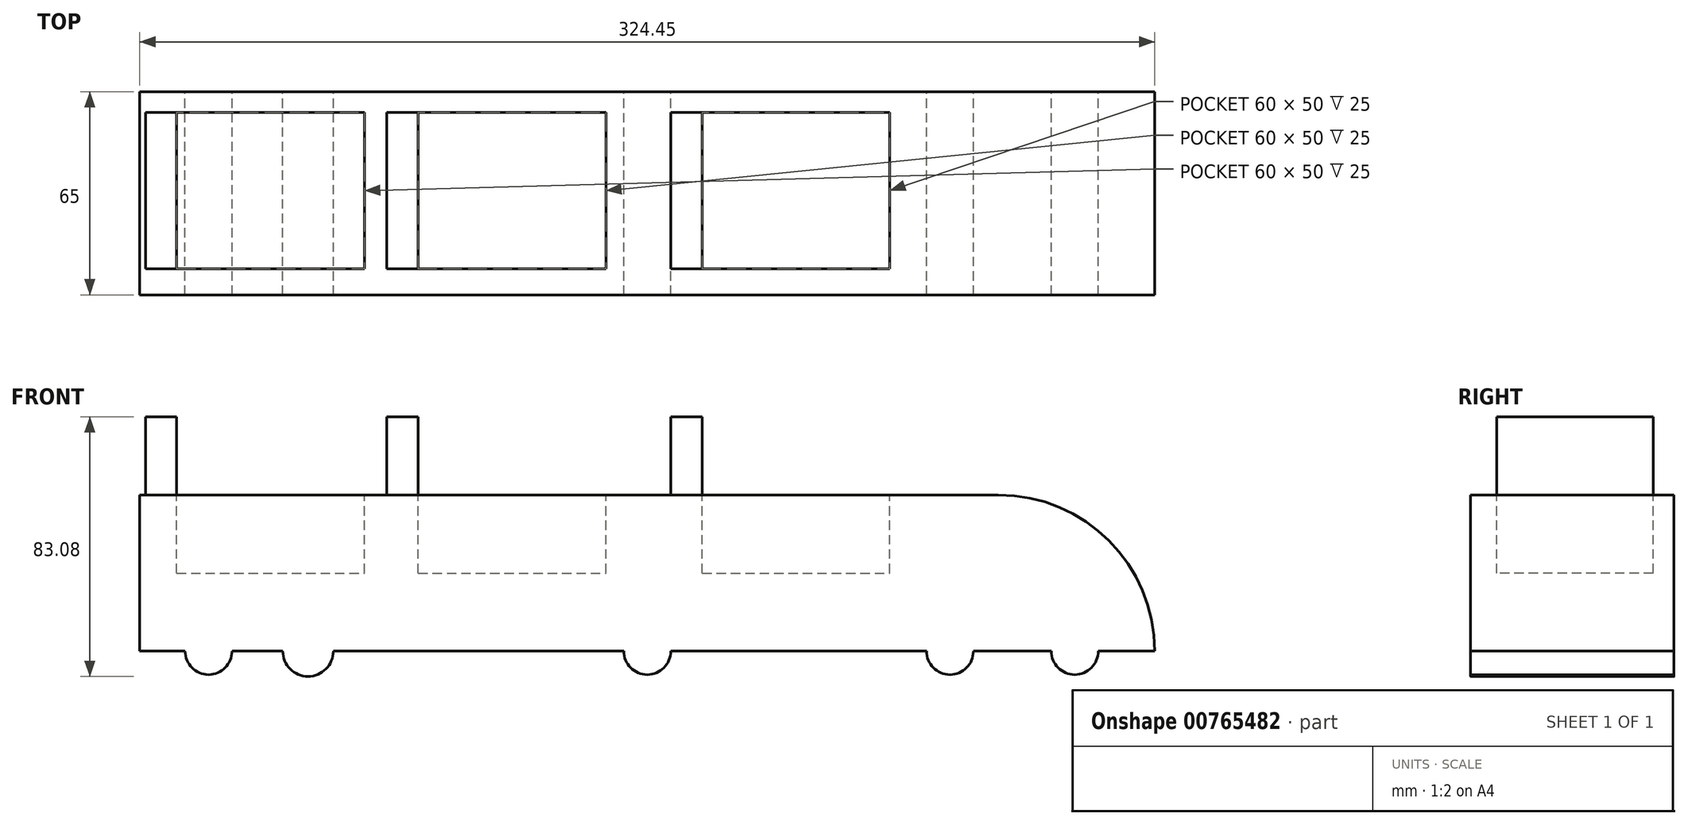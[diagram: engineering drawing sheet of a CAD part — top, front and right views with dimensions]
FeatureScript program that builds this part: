
annotation { "Feature Type Name" : "Feature", "Feature Type Description" : "" }
export const myFeature = defineFeature(function(context is Context, id is Id, definition is map)
    precondition{}
    {
        {
            var Q0;
            Q0=qCreatedBy(makeId("Top.planeOp"),FACE);
            var sketch = newSketch(context, id + "F0", { "sketchPlane" : qUnion([Q0])});
            skLineSegment(sketch, "E0.bottom", {"start": v(-92.43, -16.82) * mm, "end": v(232.02, -16.82) * mm});
            skLineSegment(sketch, "E0.top", {"start": v(-92.43, -81.82) * mm, "end": v(232.02, -81.82) * mm});
            skLineSegment(sketch, "E0.left", {"start": v(-92.43, -16.82) * mm, "end": v(-92.43, -81.82) * mm});
            skLineSegment(sketch, "E0.right", {"start": v(232.02, -16.82) * mm, "end": v(232.02, -81.82) * mm});
            skSolve(sketch);
        }
        {
            var Q0;
            Q0 = qSketchRegion(id + "F0", true);
            extrude(context, id + "F1", {"entities" : qUnion([Q0]), "depth" : 50 * mm, "offsetDistance" : 25 * mm});
        }
        {
            var Q0;
            Q0=makeQuery(id+"F1.opExtrude","CAP_EDGE",EDGE,{"disambiguationData":[OSD([sQuery(id+"F0.wireOp",EDGE,"E0.right")])],"isStart":false});
            fillet(context, id + "F2", {"entities" : qUnion([Q0]), "radius" : 50 * mm, "tangentPropagation" : true, "allowEdgeOverflow" : false});
        }
        {
            var Q0;
            Q0=makeQuery(id+"F1.opExtrude","CAP_FACE",FACE,{"disambiguationData":[OSD([sQuery(id+"F0.wireOp",EDGE,"E0.bottom"),sQuery(id+"F0.wireOp",EDGE,"E0.top"),sQuery(id+"F0.wireOp",EDGE,"E0.left"),sQuery(id+"F0.wireOp",EDGE,"E0.right")])],"isStart":false});
            var sketch = newSketch(context, id + "F3", { "sketchPlane" : qUnion([Q0])});
            skLineSegment(sketch, "E1.bottom", {"start": v(-80.63, -23.44) * mm, "end": v(-20.63, -23.44) * mm});
            skLineSegment(sketch, "E1.top", {"start": v(-80.63, -73.44) * mm, "end": v(-20.63, -73.44) * mm});
            skLineSegment(sketch, "E1.left", {"start": v(-80.63, -23.44) * mm, "end": v(-80.63, -73.44) * mm});
            skLineSegment(sketch, "E1.right", {"start": v(-20.63, -23.44) * mm, "end": v(-20.63, -73.44) * mm});
            skLineSegment(sketch, "E2.bottom", {"start": v(-3.45, -23.44) * mm, "end": v(56.55, -23.44) * mm});
            skLineSegment(sketch, "E2.top", {"start": v(-3.45, -73.44) * mm, "end": v(56.55, -73.44) * mm});
            skLineSegment(sketch, "E2.left", {"start": v(-3.45, -23.44) * mm, "end": v(-3.45, -73.44) * mm});
            skLineSegment(sketch, "E2.right", {"start": v(56.55, -23.44) * mm, "end": v(56.55, -73.44) * mm});
            skLineSegment(sketch, "E3.bottom", {"start": v(87.33, -23.44) * mm, "end": v(147.33, -23.44) * mm});
            skLineSegment(sketch, "E3.top", {"start": v(87.33, -73.44) * mm, "end": v(147.33, -73.44) * mm});
            skLineSegment(sketch, "E3.left", {"start": v(87.33, -23.44) * mm, "end": v(87.33, -73.44) * mm});
            skLineSegment(sketch, "E3.right", {"start": v(147.33, -23.44) * mm, "end": v(147.33, -73.44) * mm});
            skSolve(sketch);
        }
        {
            var Q0;
            Q0=makeQuery(id+"F3.imprint","IMPRINT",FACE,{"disambiguationData":[TD([[makeQuery(id+"F3.imprint","IMPRINT",EDGE,{"derivedFrom":sQuery(id+"F3.wireOp",EDGE,"E1.bottom")}),-1.0]])]});
            var Q1;
            Q1=makeQuery(id+"F3.imprint","IMPRINT",FACE,{"disambiguationData":[TD([[makeQuery(id+"F3.imprint","IMPRINT",EDGE,{"derivedFrom":sQuery(id+"F3.wireOp",EDGE,"E2.bottom")}),-1.0]])]});
            var Q2;
            Q2=makeQuery(id+"F3.imprint","IMPRINT",FACE,{"disambiguationData":[TD([[makeQuery(id+"F3.imprint","IMPRINT",EDGE,{"derivedFrom":sQuery(id+"F3.wireOp",EDGE,"E3.bottom")}),-1.0]])]});
            extrude(context, id + "F4", {"entities" : qUnion([Q0, Q1, Q2]), "operationType" : NewBodyOperationType.REMOVE, "oppositeDirection" : true, "depth" : 25 * mm, "offsetDistance" : 25 * mm});
        }
        {
            var Q0;
            Q0=makeQuery(id+"F1.opExtrude","SWEPT_FACE",FACE,{"disambiguationData":[OSD([sQuery(id+"F0.wireOp",EDGE,"E0.top")])]});
            var sketch = newSketch(context, id + "F5", { "sketchPlane" : qUnion([Q0])});
            skCircle(sketch, "E4", {"center": v(-77.66, 0) * mm, "radius": 7.5 * mm});
            skCircle(sketch, "E5", {"center": v(-29.66, 0) * mm, "radius": 7.5 * mm});
            skCircle(sketch, "E6", {"center": v(204.34, 0) * mm, "radius": 7.5 * mm});
            skCircle(sketch, "E7", {"center": v(157.84, 0) * mm, "radius": 7.5 * mm});
            skSolve(sketch);
        }
        {
            var Q0;
            {var subQ0=sQuery(id+"F5.wireOp",EDGE,"E6");var subQ1=makeQuery(id+"F1.opExtrude","CAP_EDGE",EDGE,{"disambiguationData":[OSD([sQuery(id+"F0.wireOp",EDGE,"E0.top")])],"isStart":true});var subQ2=makeQuery(id+"F5.imprint","INTERSECT",VERTEX,{"disambiguationData":[OD(0.0)],"derivedFrom":[subQ1,subQ0]});Q0=makeQuery(id+"F5.imprint","IMPRINT",FACE,{"disambiguationData":[TD([[makeQuery(id+"F5.imprint","IMPRINT",EDGE,{"disambiguationData":[TD([[subQ2,1.0]])],"derivedFrom":subQ0}),1.0]])]});}
            var Q1;
            {var subQ0=sQuery(id+"F5.wireOp",EDGE,"E7");var subQ1=makeQuery(id+"F1.opExtrude","CAP_EDGE",EDGE,{"disambiguationData":[OSD([sQuery(id+"F0.wireOp",EDGE,"E0.top")])],"isStart":true});var subQ2=makeQuery(id+"F5.imprint","INTERSECT",VERTEX,{"disambiguationData":[OD(0.0)],"derivedFrom":[subQ1,subQ0]});Q1=makeQuery(id+"F5.imprint","IMPRINT",FACE,{"disambiguationData":[TD([[makeQuery(id+"F5.imprint","IMPRINT",EDGE,{"disambiguationData":[TD([[subQ2,1.0]])],"derivedFrom":subQ0}),1.0]])]});}
            var Q2;
            {var subQ0=sQuery(id+"F5.wireOp",EDGE,"E5");var subQ1=makeQuery(id+"F1.opExtrude","CAP_EDGE",EDGE,{"disambiguationData":[OSD([sQuery(id+"F0.wireOp",EDGE,"E0.top")])],"isStart":true});var subQ2=makeQuery(id+"F5.imprint","INTERSECT",VERTEX,{"disambiguationData":[OD(0.0)],"derivedFrom":[subQ1,subQ0]});Q2=makeQuery(id+"F5.imprint","IMPRINT",FACE,{"disambiguationData":[TD([[makeQuery(id+"F5.imprint","IMPRINT",EDGE,{"disambiguationData":[TD([[subQ2,-1.0]])],"derivedFrom":subQ0}),1.0]])]});}
            var Q3;
            {var subQ0=sQuery(id+"F5.wireOp",EDGE,"E4");var subQ1=makeQuery(id+"F1.opExtrude","CAP_EDGE",EDGE,{"disambiguationData":[OSD([sQuery(id+"F0.wireOp",EDGE,"E0.top")])],"isStart":true});var subQ2=makeQuery(id+"F5.imprint","INTERSECT",VERTEX,{"disambiguationData":[OD(0.0)],"derivedFrom":[subQ1,subQ0]});Q3=makeQuery(id+"F5.imprint","IMPRINT",FACE,{"disambiguationData":[TD([[makeQuery(id+"F5.imprint","IMPRINT",EDGE,{"disambiguationData":[TD([[subQ2,-1.0]])],"derivedFrom":subQ0}),1.0]])]});}
            extrude(context, id + "F6", {"entities" : qUnion([Q0, Q1, Q2, Q3]), "operationType" : NewBodyOperationType.REMOVE, "depth" : 65 * mm, "offsetDistance" : 25 * mm});
        }
        {
            var Q0;
            Q0=makeQuery(id+"F1.opExtrude","SWEPT_FACE",FACE,{"disambiguationData":[OSD([sQuery(id+"F0.wireOp",EDGE,"E0.bottom")])]});
            var sketch = newSketch(context, id + "F7", { "sketchPlane" : qUnion([Q0])});
            skCircle(sketch, "E8", {"center": v(-206.44, 0) * mm, "radius": 7.5 * mm});
            skCircle(sketch, "E9", {"center": v(-166.54, 0) * mm, "radius": 7.5 * mm});
            skCircle(sketch, "E10", {"center": v(70.46, 0) * mm, "radius": 7.5 * mm});
            skCircle(sketch, "E11", {"center": v(38.66, 0) * mm, "radius": 8.08 * mm});
            skCircle(sketch, "E12", {"center": v(-69.8, 0) * mm, "radius": 7.5 * mm});
            skSolve(sketch);
        }
        {
            var Q0;
            {var subQ0=sQuery(id+"F7.wireOp",EDGE,"E8");var subQ1=makeQuery(id+"F1.opExtrude","CAP_EDGE",EDGE,{"disambiguationData":[OSD([sQuery(id+"F0.wireOp",EDGE,"E0.bottom")])],"isStart":true});var subQ2=makeQuery(id+"F7.imprint","INTERSECT",VERTEX,{"disambiguationData":[OD(0.0)],"derivedFrom":[subQ1,subQ0]});Q0=makeQuery(id+"F7.imprint","IMPRINT",FACE,{"disambiguationData":[TD([[makeQuery(id+"F7.imprint","IMPRINT",EDGE,{"disambiguationData":[TD([[subQ2,-1.0]])],"derivedFrom":subQ0}),1.0]])]});}
            var Q1;
            {var subQ0=sQuery(id+"F7.wireOp",EDGE,"E9");var subQ1=makeQuery(id+"F1.opExtrude","CAP_EDGE",EDGE,{"disambiguationData":[OSD([sQuery(id+"F0.wireOp",EDGE,"E0.bottom")])],"isStart":true});var subQ2=makeQuery(id+"F7.imprint","INTERSECT",VERTEX,{"disambiguationData":[OD(0.0)],"derivedFrom":[subQ1,subQ0]});Q1=makeQuery(id+"F7.imprint","IMPRINT",FACE,{"disambiguationData":[TD([[makeQuery(id+"F7.imprint","IMPRINT",EDGE,{"disambiguationData":[TD([[subQ2,-1.0]])],"derivedFrom":subQ0}),1.0]])]});}
            var Q2;
            {var subQ0=sQuery(id+"F7.wireOp",EDGE,"E12");var subQ1=makeQuery(id+"F1.opExtrude","CAP_EDGE",EDGE,{"disambiguationData":[OSD([sQuery(id+"F0.wireOp",EDGE,"E0.bottom")])],"isStart":true});var subQ2=makeQuery(id+"F7.imprint","INTERSECT",VERTEX,{"disambiguationData":[OD(0.0)],"derivedFrom":[subQ1,subQ0]});Q2=makeQuery(id+"F7.imprint","IMPRINT",FACE,{"disambiguationData":[TD([[makeQuery(id+"F7.imprint","IMPRINT",EDGE,{"disambiguationData":[TD([[subQ2,-1.0]])],"derivedFrom":subQ0}),1.0]])]});}
            var Q3;
            {var subQ0=sQuery(id+"F7.wireOp",EDGE,"E11");var subQ1=makeQuery(id+"F1.opExtrude","CAP_EDGE",EDGE,{"disambiguationData":[OSD([sQuery(id+"F0.wireOp",EDGE,"E0.bottom")])],"isStart":true});var subQ2=makeQuery(id+"F7.imprint","INTERSECT",VERTEX,{"disambiguationData":[OD(0.0)],"derivedFrom":[subQ1,subQ0]});Q3=makeQuery(id+"F7.imprint","IMPRINT",FACE,{"disambiguationData":[TD([[makeQuery(id+"F7.imprint","IMPRINT",EDGE,{"disambiguationData":[TD([[subQ2,1.0]])],"derivedFrom":subQ0}),1.0]])]});}
            var Q4;
            {var subQ0=sQuery(id+"F7.wireOp",EDGE,"E10");var subQ1=makeQuery(id+"F1.opExtrude","CAP_EDGE",EDGE,{"disambiguationData":[OSD([sQuery(id+"F0.wireOp",EDGE,"E0.bottom")])],"isStart":true});var subQ2=makeQuery(id+"F7.imprint","INTERSECT",VERTEX,{"disambiguationData":[OD(0.0)],"derivedFrom":[subQ1,subQ0]});Q4=makeQuery(id+"F7.imprint","IMPRINT",FACE,{"disambiguationData":[TD([[makeQuery(id+"F7.imprint","IMPRINT",EDGE,{"disambiguationData":[TD([[subQ2,1.0]])],"derivedFrom":subQ0}),1.0]])]});}
            extrude(context, id + "F8", {"entities" : qUnion([Q0, Q1, Q2, Q3, Q4]), "operationType" : NewBodyOperationType.ADD, "oppositeDirection" : true, "depth" : 65 * mm, "offsetDistance" : 25 * mm});
        }
        {
            var Q0;
            Q0=makeQuery(id+"F1.opExtrude","CAP_FACE",FACE,{"disambiguationData":[OSD([sQuery(id+"F0.wireOp",EDGE,"E0.bottom"),sQuery(id+"F0.wireOp",EDGE,"E0.top"),sQuery(id+"F0.wireOp",EDGE,"E0.left"),sQuery(id+"F0.wireOp",EDGE,"E0.right")])],"isStart":false});
            var sketch = newSketch(context, id + "F9", { "sketchPlane" : qUnion([Q0])});
            skLineSegment(sketch, "E13.bottom", {"start": v(-80.63, -23.44) * mm, "end": v(-90.63, -23.44) * mm});
            skLineSegment(sketch, "E13.top", {"start": v(-80.63, -73.44) * mm, "end": v(-90.63, -73.44) * mm});
            skLineSegment(sketch, "E13.left", {"start": v(-80.63, -23.44) * mm, "end": v(-80.63, -73.44) * mm});
            skLineSegment(sketch, "E13.right", {"start": v(-90.63, -23.44) * mm, "end": v(-90.63, -73.44) * mm});
            skLineSegment(sketch, "E14.bottom", {"start": v(-3.45, -23.44) * mm, "end": v(-13.45, -23.44) * mm});
            skLineSegment(sketch, "E14.top", {"start": v(-3.45, -73.44) * mm, "end": v(-13.45, -73.44) * mm});
            skLineSegment(sketch, "E14.left", {"start": v(-3.45, -23.44) * mm, "end": v(-3.45, -73.44) * mm});
            skLineSegment(sketch, "E14.right", {"start": v(-13.45, -23.44) * mm, "end": v(-13.45, -73.44) * mm});
            skLineSegment(sketch, "E15.bottom", {"start": v(87.33, -23.44) * mm, "end": v(77.33, -23.44) * mm});
            skLineSegment(sketch, "E15.top", {"start": v(87.33, -73.44) * mm, "end": v(77.33, -73.44) * mm});
            skLineSegment(sketch, "E15.left", {"start": v(87.33, -23.44) * mm, "end": v(87.33, -73.44) * mm});
            skLineSegment(sketch, "E15.right", {"start": v(77.33, -23.44) * mm, "end": v(77.33, -73.44) * mm});
            skSolve(sketch);
        }
        {
            var Q0;
            Q0=makeQuery(id+"F9.imprint","IMPRINT",FACE,{"disambiguationData":[TD([[makeQuery(id+"F9.imprint","IMPRINT",EDGE,{"derivedFrom":sQuery(id+"F9.wireOp",EDGE,"E13.bottom")}),1.0]])]});
            var Q1;
            Q1=makeQuery(id+"F9.imprint","IMPRINT",FACE,{"disambiguationData":[TD([[makeQuery(id+"F9.imprint","IMPRINT",EDGE,{"derivedFrom":sQuery(id+"F9.wireOp",EDGE,"E14.bottom")}),1.0]])]});
            var Q2;
            Q2=makeQuery(id+"F9.imprint","IMPRINT",FACE,{"disambiguationData":[TD([[makeQuery(id+"F9.imprint","IMPRINT",EDGE,{"derivedFrom":sQuery(id+"F9.wireOp",EDGE,"E15.bottom")}),1.0]])]});
            extrude(context, id + "F10", {"entities" : qUnion([Q0, Q1, Q2]), "operationType" : NewBodyOperationType.ADD, "depth" : 25 * mm, "offsetDistance" : 25 * mm});
        }
    });
